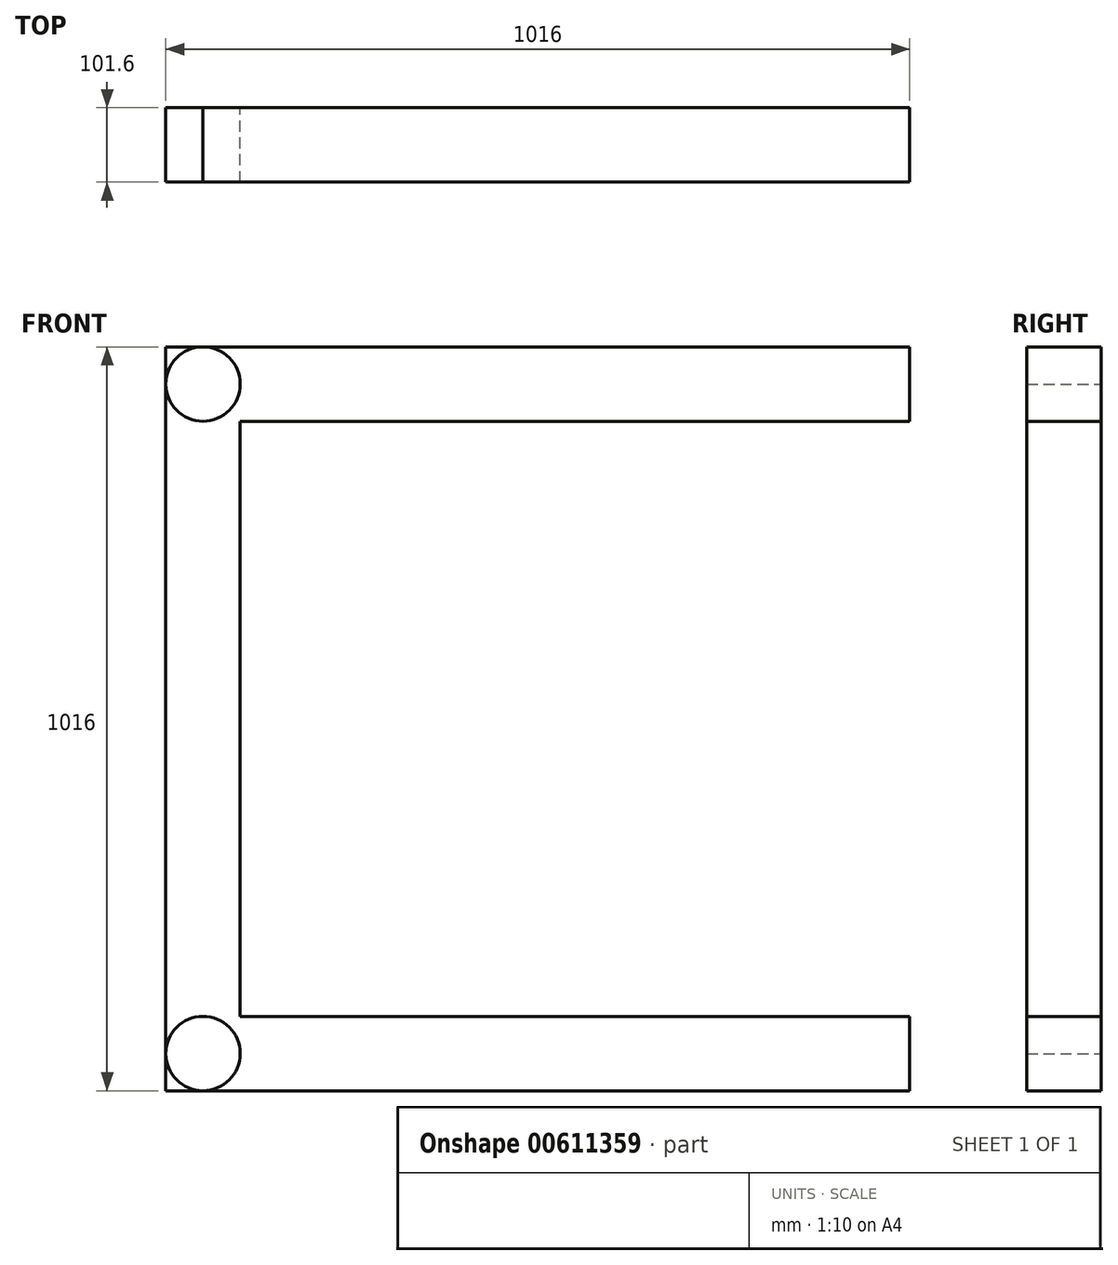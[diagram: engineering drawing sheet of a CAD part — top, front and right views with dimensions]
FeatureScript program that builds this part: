
annotation { "Feature Type Name" : "Feature", "Feature Type Description" : "" }
export const myFeature = defineFeature(function(context is Context, id is Id, definition is map)
    precondition{}
    {
        {
            var Q0;
            Q0=qCreatedBy(makeId("Front.planeOp"),FACE);
            var sketch = newSketch(context, id + "F0", { "sketchPlane" : qUnion([Q0])});
            skLineSegment(sketch, "E0.bottom", {"start": v(-599.03, 500.14) * mm, "end": v(416.97, 500.14) * mm});
            skLineSegment(sketch, "E0.top", {"start": v(-599.03, 398.54) * mm, "end": v(416.97, 398.54) * mm});
            skLineSegment(sketch, "E0.left", {"start": v(-599.03, 500.14) * mm, "end": v(-599.03, 398.54) * mm});
            skLineSegment(sketch, "E0.right", {"start": v(416.97, 500.14) * mm, "end": v(416.97, 398.54) * mm});
            skLineSegment(sketch, "E1.bottom", {"start": v(-599.03, 398.54) * mm, "end": v(-497.43, 398.54) * mm});
            skLineSegment(sketch, "E1.top", {"start": v(-599.03, -414.26) * mm, "end": v(-497.43, -414.26) * mm});
            skLineSegment(sketch, "E1.left", {"start": v(-599.03, 398.54) * mm, "end": v(-599.03, -414.26) * mm});
            skLineSegment(sketch, "E1.right", {"start": v(-497.43, 398.54) * mm, "end": v(-497.43, -414.26) * mm});
            skLineSegment(sketch, "E2.bottom", {"start": v(-599.03, -414.26) * mm, "end": v(416.97, -414.26) * mm});
            skLineSegment(sketch, "E2.top", {"start": v(-599.03, -515.86) * mm, "end": v(416.97, -515.86) * mm});
            skLineSegment(sketch, "E2.left", {"start": v(-599.03, -414.26) * mm, "end": v(-599.03, -515.86) * mm});
            skLineSegment(sketch, "E2.right", {"start": v(416.97, -414.26) * mm, "end": v(416.97, -515.86) * mm});
            skCircle(sketch, "E3", {"center": v(-548.23, 449.34) * mm, "radius": 50.8 * mm});
            skCircle(sketch, "E4", {"center": v(-548.23, -465.06) * mm, "radius": 50.8 * mm});
            skSolve(sketch);
        }
        {
            var Q0;
            {var subQ2=sQuery(id+"F0.wireOp",EDGE,"E0.top");Q0=makeQuery(id+"F0.imprint","IMPRINT",FACE,{"disambiguationData":[TD([[makeQuery(id+"F0.imprint","IMPRINT",EDGE,{"derivedFrom":subQ2}),1.0]])]});}
            var Q1;
            {var subQ0=sQuery(id+"F0.wireOp",EDGE,"E0.left");var subQ1=sQuery(id+"F0.wireOp",EDGE,"E0.bottom");var subQ2=makeQuery(id+"F0.imprint","INTERSECT",VERTEX,{"derivedFrom":[subQ1,subQ0]});Q1=makeQuery(id+"F0.imprint","IMPRINT",FACE,{"disambiguationData":[TD([[makeQuery(id+"F0.imprint","IMPRINT",EDGE,{"disambiguationData":[TD([[subQ2,-1.0]])],"derivedFrom":subQ1}),-1.0]])]});}
            var Q2;
            {var subQ1=sQuery(id+"F0.wireOp",EDGE,"E0.left");var subQ3=sQuery(id+"F0.wireOp",EDGE,"E3");var subQ4=makeQuery(id+"F0.imprint","INTERSECT",VERTEX,{"derivedFrom":[subQ1,subQ3]});Q2=makeQuery(id+"F0.imprint","IMPRINT",FACE,{"disambiguationData":[TD([[makeQuery(id+"F0.imprint","IMPRINT",EDGE,{"disambiguationData":[TD([[subQ4,-1.0]])],"derivedFrom":subQ3}),-1.0]])]});}
            var Q3;
            {var subQ1=sQuery(id+"F0.wireOp",EDGE,"E1.left");Q3=makeQuery(id+"F0.imprint","IMPRINT",FACE,{"disambiguationData":[TD([[makeQuery(id+"F0.imprint","IMPRINT",EDGE,{"derivedFrom":subQ1}),1.0]])]});}
            var Q4;
            {var subQ0=sQuery(id+"F0.wireOp",EDGE,"E2.right");Q4=makeQuery(id+"F0.imprint","IMPRINT",FACE,{"disambiguationData":[TD([[makeQuery(id+"F0.imprint","IMPRINT",EDGE,{"derivedFrom":subQ0}),-1.0]])]});}
            var Q5;
            {var subQ0=sQuery(id+"F0.wireOp",EDGE,"E2.left");var subQ1=sQuery(id+"F0.wireOp",EDGE,"E2.top");var subQ2=makeQuery(id+"F0.imprint","INTERSECT",VERTEX,{"derivedFrom":[subQ1,subQ0]});Q5=makeQuery(id+"F0.imprint","IMPRINT",FACE,{"disambiguationData":[TD([[makeQuery(id+"F0.imprint","IMPRINT",EDGE,{"disambiguationData":[TD([[subQ2,-1.0]])],"derivedFrom":subQ1}),1.0]])]});}
            var Q6;
            {var subQ0=sQuery(id+"F0.wireOp",EDGE,"E2.left");var subQ3=sQuery(id+"F0.wireOp",EDGE,"E4");var subQ5=makeQuery(id+"F0.imprint","INTERSECT",VERTEX,{"derivedFrom":[subQ0,subQ3]});Q6=makeQuery(id+"F0.imprint","IMPRINT",FACE,{"disambiguationData":[TD([[makeQuery(id+"F0.imprint","IMPRINT",EDGE,{"disambiguationData":[TD([[subQ5,1.0]])],"derivedFrom":subQ3}),-1.0]])]});}
            extrude(context, id + "F1", {"entities" : qUnion([Q0, Q1, Q2, Q3, Q4, Q5, Q6]), "depth" : 101.6 * mm, "offsetDistance" : 25.4 * mm});
        }
    });
